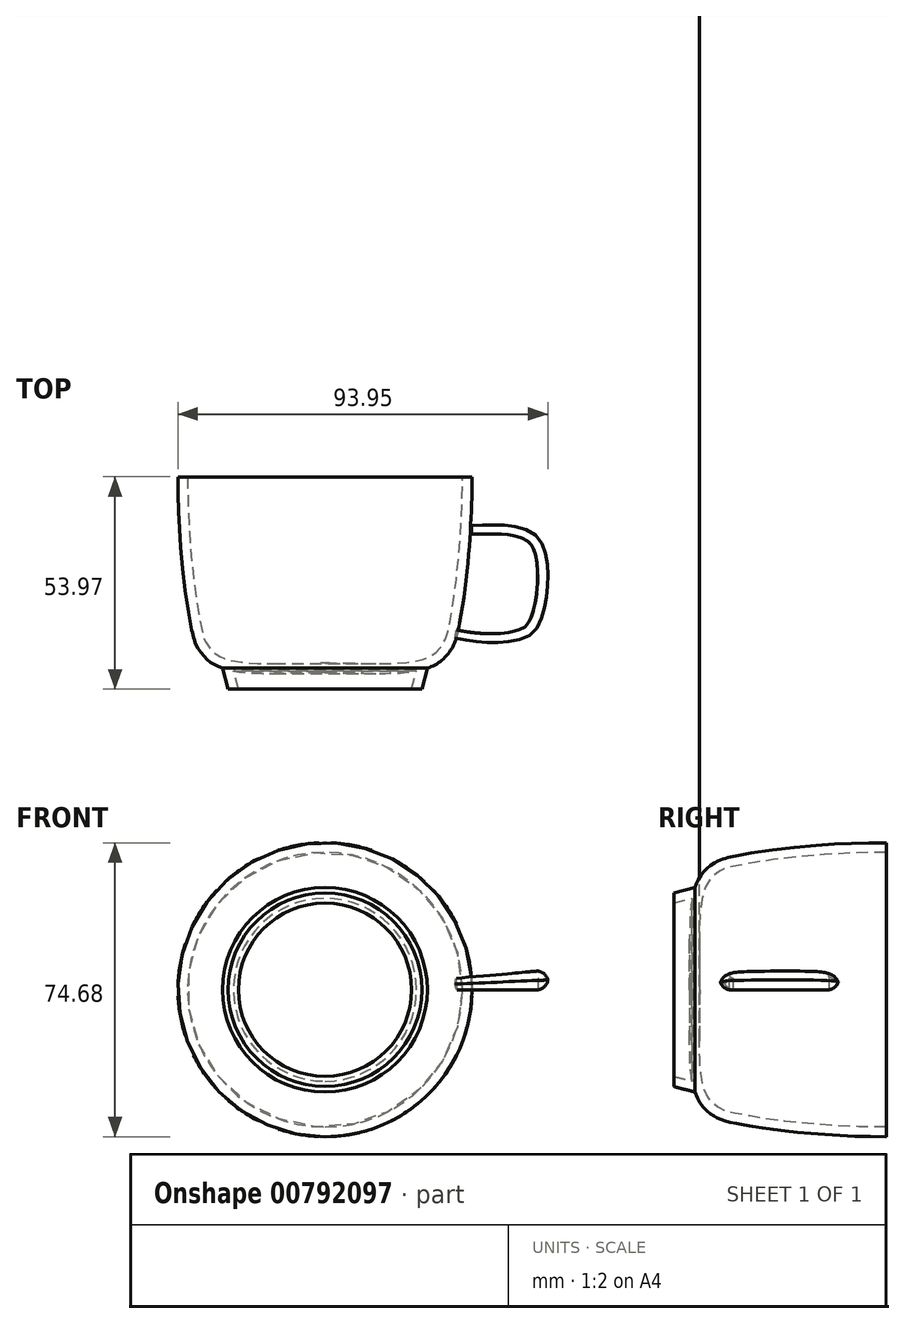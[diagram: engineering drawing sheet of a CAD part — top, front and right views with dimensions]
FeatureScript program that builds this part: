
annotation { "Feature Type Name" : "Feature", "Feature Type Description" : "" }
export const myFeature = defineFeature(function(context is Context, id is Id, definition is map)
    precondition{}
    {
        {
            var Q0;
            Q0=qCreatedBy(makeId("Top.planeOp"),FACE);
            var sketch = newSketch(context, id + "F0", { "sketchPlane" : qUnion([Q0])});
            skFitSpline(sketch, "E0", {"points": [v(0, -45.68) * mm, v(26, -44.55) * mm, v(31.9, -40.05) * mm, v(33.87, -34.71) * mm, v(37.24, 9.7) * mm], "startDerivative": vector(96.2, 0) * mm, "endDerivative": vector(-4.8, 143.62) * mm});
            skFitSpline(sketch, "E1.0", {"points": [v(0, -43.18) * mm, v(2.03, -43.18) * mm, v(6.14, -43.25) * mm, v(11.15, -43.35) * mm, v(14.93, -43.35) * mm, v(17.6, -43.29) * mm, v(20.07, -43.13) * mm, v(21.92, -42.92) * mm, v(23.24, -42.7) * mm, v(24.15, -42.5) * mm, v(24.97, -42.27) * mm, v(25.92, -41.93) * mm, v(26.94, -41.44) * mm, v(27.92, -40.78) * mm, v(28.59, -40.18) * mm, v(29.05, -39.69) * mm, v(29.37, -39.3) * mm, v(29.65, -38.92) * mm, v(29.91, -38.53) * mm, v(30.13, -38.17) * mm, v(30.39, -37.7) * mm, v(30.66, -37.1) * mm, v(30.97, -36.14) * mm, v(31.3, -34.83) * mm, v(31.66, -33.08) * mm, v(32.05, -30.94) * mm, v(32.6, -27.6) * mm, v(33.3, -22.6) * mm, v(34.03, -15.54) * mm, v(34.6, -7.66) * mm, v(34.89, 0.8) * mm, v(34.84, 6.66) * mm, v(34.74, 9.61) * mm]});
            skLineSegment(sketch, "E2", {"start": v(34.84, 4.08) * mm, "end": v(37.34, 4.08) * mm});
            skLineSegment(sketch, "E3", {"start": v(0, -49.9) * mm, "end": v(0, -43.18) * mm});
            skFitSpline(sketch, "E4", {"points": [v(0, -49.9) * mm, v(24.6, -49.9) * mm], "startDerivative": vector(24.6, 0) * mm, "endDerivative": vector(24.6, 0) * mm});
            skLineSegment(sketch, "E5", {"start": v(26, -44.55) * mm, "end": v(24.6, -49.9) * mm});
            skSolve(sketch);
        }
        {
            var Q0;
            {var subQ1=sQuery(id+"F0.wireOp",EDGE,"E0");var subQ5=sQuery(id+"F0.wireOp",EDGE,"E3");var subQ8=makeQuery(id+"F0.imprint","INTERSECT",VERTEX,{"derivedFrom":[subQ1,subQ5]});Q0=makeQuery(id+"F0.imprint","IMPRINT",FACE,{"disambiguationData":[TD([[makeQuery(id+"F0.imprint","IMPRINT",EDGE,{"disambiguationData":[TD([[subQ8,-1.0]])],"derivedFrom":subQ1}),1.0]])]});}
            var Q1;
            {var subQ4=sQuery(id+"F0.wireOp",EDGE,"E4");Q1=makeQuery(id+"F0.imprint","IMPRINT",FACE,{"disambiguationData":[TD([[makeQuery(id+"F0.imprint","IMPRINT",EDGE,{"derivedFrom":subQ4}),1.0]])]});}
            var Q2;
            Q2=sQuery(id+"F0.wireOp",EDGE,"E3");
            revolve(context, id + "F1", {"surfaceOperationType" : NewSurfaceOperationType.NEW, "entities" : qUnion([Q0, Q1]), "axis" : qUnion([Q2]), "revolveType" : RevolveType.FULL});
        }
        {
            var Q0;
            Q0=makeQuery(id+"F1.opRevolve","SWEPT_FACE",FACE,{"disambiguationData":[OSD([sQuery(id+"F0.wireOp",EDGE,"E4")])]});
            shell(context, id + "F2", {"entities" : qUnion([Q0]), "thickness" : 2.5 * mm});
        }
        {
            var Q0;
            Q0=qCreatedBy(makeId("Top.planeOp"),FACE);
            var sketch = newSketch(context, id + "F3", { "sketchPlane" : qUnion([Q0])});
            skFitSpline(sketch, "E6", {"points": [v(37.24, -8.01) * mm, v(49.05, -8.57) * mm, v(55.23, -12.79) * mm, v(54.67, -33.03) * mm, v(49.05, -37.52) * mm, v(33.03, -37.24) * mm], "startDerivative": vector(118.58, 3.49) * mm, "endDerivative": vector(-91.42, 18.28) * mm});
            skFitSpline(sketch, "E7.0", {"points": [v(37.32, -10.5) * mm, v(38.54, -10.47) * mm, v(40.68, -10.42) * mm, v(43.08, -10.4) * mm, v(44.83, -10.44) * mm, v(46.1, -10.54) * mm, v(46.92, -10.66) * mm, v(47.56, -10.79) * mm, v(47.98, -10.88) * mm, v(48.34, -10.97) * mm, v(48.72, -11.07) * mm, v(49.2, -11.2) * mm, v(49.74, -11.36) * mm, v(50.45, -11.61) * mm, v(51.26, -12) * mm, v(51.95, -12.51) * mm, v(52.43, -13.03) * mm, v(52.71, -13.41) * mm, v(52.93, -13.77) * mm, v(53.13, -14.16) * mm, v(53.37, -14.76) * mm, v(53.64, -15.63) * mm, v(53.93, -16.95) * mm, v(54.18, -18.85) * mm, v(54.26, -21.37) * mm, v(54.15, -23.98) * mm, v(53.86, -26.56) * mm, v(53.48, -28.55) * mm, v(53.11, -29.97) * mm, v(52.81, -30.93) * mm, v(52.5, -31.77) * mm, v(52.18, -32.46) * mm, v(51.86, -33) * mm, v(51.45, -33.58) * mm, v(50.94, -34.08) * mm, v(50.24, -34.52) * mm, v(49.43, -34.83) * mm, v(48.72, -35.03) * mm, v(48.27, -35.14) * mm, v(47.59, -35.3) * mm, v(46.47, -35.5) * mm, v(44.8, -35.69) * mm, v(42.93, -35.77) * mm, v(40.88, -35.74) * mm, v(37.89, -35.53) * mm, v(35.35, -35.16) * mm, v(33.52, -34.8) * mm]});
            skLineSegment(sketch, "E8", {"start": v(37.24, -8.01) * mm, "end": v(37.32, -10.5) * mm});
            skLineSegment(sketch, "E9", {"start": v(33.52, -34.8) * mm, "end": v(33.03, -37.24) * mm});
            skSolve(sketch);
        }
        {
            var Q0;
            Q0=makeQuery(id+"F3.imprint","IMPRINT",FACE,{"disambiguationData":[TD([[makeQuery(id+"F3.imprint","IMPRINT",EDGE,{"derivedFrom":sQuery(id+"F3.wireOp",EDGE,"E6")}),-1.0]])]});
            var Q1;
            Q1=makeQuery(id+"F1.opRevolve","SWEPT_FACE",FACE,{"disambiguationData":[OSD([sQuery(id+"F0.wireOp",EDGE,"E0")])]});
            revolve(context, id + "F4", {"surfaceOperationType" : NewSurfaceOperationType.NEW, "entities" : qUnion([Q0]), "axis" : qUnion([Q1]), "revolveType" : RevolveType.ONE_DIRECTION, "angle" : 5 * degree});
        }
        {
            var Q0;
            Q0=makeQuery(id+"F4.opRevolve","CAP_EDGE",EDGE,{"disambiguationData":[OSD([sQuery(id+"F3.wireOp",EDGE,"E6")])],"isStart":true});
            var Q1;
            Q1=makeQuery(id+"F4.opRevolve","CAP_EDGE",EDGE,{"disambiguationData":[OSD([sQuery(id+"F3.wireOp",EDGE,"E6")])],"isStart":false});
            fillet(context, id + "F5", {"entities" : qUnion([Q0, Q1]), "radius" : 3 * mm, "tangentPropagation" : true, "allowEdgeOverflow" : false});
        }
        {
            var Q0;
            Q0=qCreatedBy(makeId("Top.planeOp"),FACE);
            var sketch = newSketch(context, id + "F6", { "sketchPlane" : qUnion([Q0])});
            skText(sketch, "E10", { "text": "sgw", "fontName": "OpenSans-Regular.ttf"});
            const initialGuessF6  = {"E10": [-0.017, -0.03303, 1, 0, 0.01799]};
            skSetInitialGuess(sketch, initialGuessF6);
            skSolve(sketch);
        }
        {
            var Q0;
            Q0 = qSketchRegion(id + "F6", true);
            extrude(context, id + "F7", {"entities" : qUnion([Q0]), "depth" : 36 * mm, "offsetDistance" : 25 * mm});
        }
        {
            var Q0;
            Q0=makeQuery(id+"F1.opRevolve","SWEPT_BODY",BODY,{"disambiguationData":[OSD([sQuery(id+"F0.wireOp",EDGE,"E0"),sQuery(id+"F0.wireOp",EDGE,"E1.0"),sQuery(id+"F0.wireOp",EDGE,"E2"),sQuery(id+"F0.wireOp",EDGE,"E3"),sQuery(id+"F0.wireOp",EDGE,"E4"),sQuery(id+"F0.wireOp",EDGE,"E5")])]});
            var Q1;
            Q1=makeQuery(id+"F7.opExtrude","SWEPT_BODY",BODY,{"disambiguationData":[OSD([sQuery(id+"F6.wireOp",EDGE,"E10.sketch_text.stroke-69"),sQuery(id+"F6.wireOp",EDGE,"E10.sketch_text.stroke-70"),sQuery(id+"F6.wireOp",EDGE,"E10.sketch_text.stroke-71"),sQuery(id+"F6.wireOp",EDGE,"E10.sketch_text.stroke-72"),sQuery(id+"F6.wireOp",EDGE,"E10.sketch_text.stroke-73"),sQuery(id+"F6.wireOp",EDGE,"E10.sketch_text.stroke-74"),sQuery(id+"F6.wireOp",EDGE,"E10.sketch_text.stroke-75"),sQuery(id+"F6.wireOp",EDGE,"E10.sketch_text.stroke-76"),sQuery(id+"F6.wireOp",EDGE,"E10.sketch_text.stroke-77"),sQuery(id+"F6.wireOp",EDGE,"E10.sketch_text.stroke-78"),sQuery(id+"F6.wireOp",EDGE,"E10.sketch_text.stroke-79"),sQuery(id+"F6.wireOp",EDGE,"E10.sketch_text.stroke-80"),sQuery(id+"F6.wireOp",EDGE,"E10.sketch_text.stroke-81"),sQuery(id+"F6.wireOp",EDGE,"E10.sketch_text.stroke-82"),sQuery(id+"F6.wireOp",EDGE,"E10.sketch_text.stroke-83"),sQuery(id+"F6.wireOp",EDGE,"E10.sketch_text.stroke-84"),sQuery(id+"F6.wireOp",EDGE,"E10.sketch_text.stroke-85"),sQuery(id+"F6.wireOp",EDGE,"E10.sketch_text.stroke-86"),sQuery(id+"F6.wireOp",EDGE,"E10.sketch_text.stroke-87"),sQuery(id+"F6.wireOp",EDGE,"E10.sketch_text.stroke-88"),sQuery(id+"F6.wireOp",EDGE,"E10.sketch_text.stroke-89"),sQuery(id+"F6.wireOp",EDGE,"E10.sketch_text.stroke-90"),sQuery(id+"F6.wireOp",EDGE,"E10.sketch_text.stroke-91")])]});
            var Q2;
            Q2=makeQuery(id+"F7.opExtrude","SWEPT_BODY",BODY,{"disambiguationData":[OSD([sQuery(id+"F6.wireOp",EDGE,"E10.sketch_text.stroke-25"),sQuery(id+"F6.wireOp",EDGE,"E10.sketch_text.stroke-26"),sQuery(id+"F6.wireOp",EDGE,"E10.sketch_text.stroke-27"),sQuery(id+"F6.wireOp",EDGE,"E10.sketch_text.stroke-28"),sQuery(id+"F6.wireOp",EDGE,"E10.sketch_text.stroke-29"),sQuery(id+"F6.wireOp",EDGE,"E10.sketch_text.stroke-30"),sQuery(id+"F6.wireOp",EDGE,"E10.sketch_text.stroke-31"),sQuery(id+"F6.wireOp",EDGE,"E10.sketch_text.stroke-32"),sQuery(id+"F6.wireOp",EDGE,"E10.sketch_text.stroke-33"),sQuery(id+"F6.wireOp",EDGE,"E10.sketch_text.stroke-34"),sQuery(id+"F6.wireOp",EDGE,"E10.sketch_text.stroke-35"),sQuery(id+"F6.wireOp",EDGE,"E10.sketch_text.stroke-36"),sQuery(id+"F6.wireOp",EDGE,"E10.sketch_text.stroke-37"),sQuery(id+"F6.wireOp",EDGE,"E10.sketch_text.stroke-38"),sQuery(id+"F6.wireOp",EDGE,"E10.sketch_text.stroke-39"),sQuery(id+"F6.wireOp",EDGE,"E10.sketch_text.stroke-40"),sQuery(id+"F6.wireOp",EDGE,"E10.sketch_text.stroke-41"),sQuery(id+"F6.wireOp",EDGE,"E10.sketch_text.stroke-42"),sQuery(id+"F6.wireOp",EDGE,"E10.sketch_text.stroke-43"),sQuery(id+"F6.wireOp",EDGE,"E10.sketch_text.stroke-44"),sQuery(id+"F6.wireOp",EDGE,"E10.sketch_text.stroke-45"),sQuery(id+"F6.wireOp",EDGE,"E10.sketch_text.stroke-46"),sQuery(id+"F6.wireOp",EDGE,"E10.sketch_text.stroke-47"),sQuery(id+"F6.wireOp",EDGE,"E10.sketch_text.stroke-48"),sQuery(id+"F6.wireOp",EDGE,"E10.sketch_text.stroke-49"),sQuery(id+"F6.wireOp",EDGE,"E10.sketch_text.stroke-50"),sQuery(id+"F6.wireOp",EDGE,"E10.sketch_text.stroke-51"),sQuery(id+"F6.wireOp",EDGE,"E10.sketch_text.stroke-52"),sQuery(id+"F6.wireOp",EDGE,"E10.sketch_text.stroke-53"),sQuery(id+"F6.wireOp",EDGE,"E10.sketch_text.stroke-54"),sQuery(id+"F6.wireOp",EDGE,"E10.sketch_text.stroke-55"),sQuery(id+"F6.wireOp",EDGE,"E10.sketch_text.stroke-56"),sQuery(id+"F6.wireOp",EDGE,"E10.sketch_text.stroke-57"),sQuery(id+"F6.wireOp",EDGE,"E10.sketch_text.stroke-58"),sQuery(id+"F6.wireOp",EDGE,"E10.sketch_text.stroke-59"),sQuery(id+"F6.wireOp",EDGE,"E10.sketch_text.stroke-60"),sQuery(id+"F6.wireOp",EDGE,"E10.sketch_text.stroke-61"),sQuery(id+"F6.wireOp",EDGE,"E10.sketch_text.stroke-62"),sQuery(id+"F6.wireOp",EDGE,"E10.sketch_text.stroke-63"),sQuery(id+"F6.wireOp",EDGE,"E10.sketch_text.stroke-64"),sQuery(id+"F6.wireOp",EDGE,"E10.sketch_text.stroke-65"),sQuery(id+"F6.wireOp",EDGE,"E10.sketch_text.stroke-66"),sQuery(id+"F6.wireOp",EDGE,"E10.sketch_text.stroke-67"),sQuery(id+"F6.wireOp",EDGE,"E10.sketch_text.stroke-68")])]});
            var Q3;
            Q3=makeQuery(id+"F7.opExtrude","SWEPT_BODY",BODY,{"disambiguationData":[OSD([sQuery(id+"F6.wireOp",EDGE,"E10.sketch_text.stroke-0"),sQuery(id+"F6.wireOp",EDGE,"E10.sketch_text.stroke-1"),sQuery(id+"F6.wireOp",EDGE,"E10.sketch_text.stroke-2"),sQuery(id+"F6.wireOp",EDGE,"E10.sketch_text.stroke-3"),sQuery(id+"F6.wireOp",EDGE,"E10.sketch_text.stroke-4"),sQuery(id+"F6.wireOp",EDGE,"E10.sketch_text.stroke-5"),sQuery(id+"F6.wireOp",EDGE,"E10.sketch_text.stroke-6"),sQuery(id+"F6.wireOp",EDGE,"E10.sketch_text.stroke-7"),sQuery(id+"F6.wireOp",EDGE,"E10.sketch_text.stroke-8"),sQuery(id+"F6.wireOp",EDGE,"E10.sketch_text.stroke-9"),sQuery(id+"F6.wireOp",EDGE,"E10.sketch_text.stroke-10"),sQuery(id+"F6.wireOp",EDGE,"E10.sketch_text.stroke-11"),sQuery(id+"F6.wireOp",EDGE,"E10.sketch_text.stroke-12"),sQuery(id+"F6.wireOp",EDGE,"E10.sketch_text.stroke-13"),sQuery(id+"F6.wireOp",EDGE,"E10.sketch_text.stroke-14"),sQuery(id+"F6.wireOp",EDGE,"E10.sketch_text.stroke-15"),sQuery(id+"F6.wireOp",EDGE,"E10.sketch_text.stroke-16"),sQuery(id+"F6.wireOp",EDGE,"E10.sketch_text.stroke-17"),sQuery(id+"F6.wireOp",EDGE,"E10.sketch_text.stroke-18"),sQuery(id+"F6.wireOp",EDGE,"E10.sketch_text.stroke-19"),sQuery(id+"F6.wireOp",EDGE,"E10.sketch_text.stroke-20"),sQuery(id+"F6.wireOp",EDGE,"E10.sketch_text.stroke-21"),sQuery(id+"F6.wireOp",EDGE,"E10.sketch_text.stroke-22"),sQuery(id+"F6.wireOp",EDGE,"E10.sketch_text.stroke-23"),sQuery(id+"F6.wireOp",EDGE,"E10.sketch_text.stroke-24")])]});
            booleanBodies(context, id + "F8", {"operationType" : BooleanOperationType.SUBTRACTION, "tools" : qUnion([Q0]), "targets" : qUnion([Q1, Q2, Q3]), "keepTools" : true});
        }
        {
            var Q0;
            Q0=makeQuery(id+"F8.opBoolean","SPLIT",BODY,{"disambiguationData":[OD(0.0)],"derivedFrom":makeQuery(id+"F7.opExtrude","SWEPT_BODY",BODY,{"disambiguationData":[OSD([sQuery(id+"F6.wireOp",EDGE,"E10.sketch_text.stroke-0"),sQuery(id+"F6.wireOp",EDGE,"E10.sketch_text.stroke-1"),sQuery(id+"F6.wireOp",EDGE,"E10.sketch_text.stroke-2"),sQuery(id+"F6.wireOp",EDGE,"E10.sketch_text.stroke-3"),sQuery(id+"F6.wireOp",EDGE,"E10.sketch_text.stroke-4"),sQuery(id+"F6.wireOp",EDGE,"E10.sketch_text.stroke-5"),sQuery(id+"F6.wireOp",EDGE,"E10.sketch_text.stroke-6"),sQuery(id+"F6.wireOp",EDGE,"E10.sketch_text.stroke-7"),sQuery(id+"F6.wireOp",EDGE,"E10.sketch_text.stroke-8"),sQuery(id+"F6.wireOp",EDGE,"E10.sketch_text.stroke-9"),sQuery(id+"F6.wireOp",EDGE,"E10.sketch_text.stroke-10"),sQuery(id+"F6.wireOp",EDGE,"E10.sketch_text.stroke-11"),sQuery(id+"F6.wireOp",EDGE,"E10.sketch_text.stroke-12"),sQuery(id+"F6.wireOp",EDGE,"E10.sketch_text.stroke-13"),sQuery(id+"F6.wireOp",EDGE,"E10.sketch_text.stroke-14"),sQuery(id+"F6.wireOp",EDGE,"E10.sketch_text.stroke-15"),sQuery(id+"F6.wireOp",EDGE,"E10.sketch_text.stroke-16"),sQuery(id+"F6.wireOp",EDGE,"E10.sketch_text.stroke-17"),sQuery(id+"F6.wireOp",EDGE,"E10.sketch_text.stroke-18"),sQuery(id+"F6.wireOp",EDGE,"E10.sketch_text.stroke-19"),sQuery(id+"F6.wireOp",EDGE,"E10.sketch_text.stroke-20"),sQuery(id+"F6.wireOp",EDGE,"E10.sketch_text.stroke-21"),sQuery(id+"F6.wireOp",EDGE,"E10.sketch_text.stroke-22"),sQuery(id+"F6.wireOp",EDGE,"E10.sketch_text.stroke-23"),sQuery(id+"F6.wireOp",EDGE,"E10.sketch_text.stroke-24")])]})});
            var Q1;
            Q1=makeQuery(id+"F8.opBoolean","SPLIT",BODY,{"disambiguationData":[OD(0.0)],"derivedFrom":makeQuery(id+"F7.opExtrude","SWEPT_BODY",BODY,{"disambiguationData":[OSD([sQuery(id+"F6.wireOp",EDGE,"E10.sketch_text.stroke-25"),sQuery(id+"F6.wireOp",EDGE,"E10.sketch_text.stroke-26"),sQuery(id+"F6.wireOp",EDGE,"E10.sketch_text.stroke-27"),sQuery(id+"F6.wireOp",EDGE,"E10.sketch_text.stroke-28"),sQuery(id+"F6.wireOp",EDGE,"E10.sketch_text.stroke-29"),sQuery(id+"F6.wireOp",EDGE,"E10.sketch_text.stroke-30"),sQuery(id+"F6.wireOp",EDGE,"E10.sketch_text.stroke-31"),sQuery(id+"F6.wireOp",EDGE,"E10.sketch_text.stroke-32"),sQuery(id+"F6.wireOp",EDGE,"E10.sketch_text.stroke-33"),sQuery(id+"F6.wireOp",EDGE,"E10.sketch_text.stroke-34"),sQuery(id+"F6.wireOp",EDGE,"E10.sketch_text.stroke-35"),sQuery(id+"F6.wireOp",EDGE,"E10.sketch_text.stroke-36"),sQuery(id+"F6.wireOp",EDGE,"E10.sketch_text.stroke-37"),sQuery(id+"F6.wireOp",EDGE,"E10.sketch_text.stroke-38"),sQuery(id+"F6.wireOp",EDGE,"E10.sketch_text.stroke-39"),sQuery(id+"F6.wireOp",EDGE,"E10.sketch_text.stroke-40"),sQuery(id+"F6.wireOp",EDGE,"E10.sketch_text.stroke-41"),sQuery(id+"F6.wireOp",EDGE,"E10.sketch_text.stroke-42"),sQuery(id+"F6.wireOp",EDGE,"E10.sketch_text.stroke-43"),sQuery(id+"F6.wireOp",EDGE,"E10.sketch_text.stroke-44"),sQuery(id+"F6.wireOp",EDGE,"E10.sketch_text.stroke-45"),sQuery(id+"F6.wireOp",EDGE,"E10.sketch_text.stroke-46"),sQuery(id+"F6.wireOp",EDGE,"E10.sketch_text.stroke-47"),sQuery(id+"F6.wireOp",EDGE,"E10.sketch_text.stroke-48"),sQuery(id+"F6.wireOp",EDGE,"E10.sketch_text.stroke-49"),sQuery(id+"F6.wireOp",EDGE,"E10.sketch_text.stroke-50"),sQuery(id+"F6.wireOp",EDGE,"E10.sketch_text.stroke-51"),sQuery(id+"F6.wireOp",EDGE,"E10.sketch_text.stroke-52"),sQuery(id+"F6.wireOp",EDGE,"E10.sketch_text.stroke-53"),sQuery(id+"F6.wireOp",EDGE,"E10.sketch_text.stroke-54"),sQuery(id+"F6.wireOp",EDGE,"E10.sketch_text.stroke-55"),sQuery(id+"F6.wireOp",EDGE,"E10.sketch_text.stroke-56"),sQuery(id+"F6.wireOp",EDGE,"E10.sketch_text.stroke-57"),sQuery(id+"F6.wireOp",EDGE,"E10.sketch_text.stroke-58"),sQuery(id+"F6.wireOp",EDGE,"E10.sketch_text.stroke-59"),sQuery(id+"F6.wireOp",EDGE,"E10.sketch_text.stroke-60"),sQuery(id+"F6.wireOp",EDGE,"E10.sketch_text.stroke-61"),sQuery(id+"F6.wireOp",EDGE,"E10.sketch_text.stroke-62"),sQuery(id+"F6.wireOp",EDGE,"E10.sketch_text.stroke-63"),sQuery(id+"F6.wireOp",EDGE,"E10.sketch_text.stroke-64"),sQuery(id+"F6.wireOp",EDGE,"E10.sketch_text.stroke-65"),sQuery(id+"F6.wireOp",EDGE,"E10.sketch_text.stroke-66"),sQuery(id+"F6.wireOp",EDGE,"E10.sketch_text.stroke-67"),sQuery(id+"F6.wireOp",EDGE,"E10.sketch_text.stroke-68")])]})});
            var Q2;
            Q2=makeQuery(id+"F8.opBoolean","SPLIT",BODY,{"disambiguationData":[OD(0.0)],"derivedFrom":makeQuery(id+"F7.opExtrude","SWEPT_BODY",BODY,{"disambiguationData":[OSD([sQuery(id+"F6.wireOp",EDGE,"E10.sketch_text.stroke-69"),sQuery(id+"F6.wireOp",EDGE,"E10.sketch_text.stroke-70"),sQuery(id+"F6.wireOp",EDGE,"E10.sketch_text.stroke-71"),sQuery(id+"F6.wireOp",EDGE,"E10.sketch_text.stroke-72"),sQuery(id+"F6.wireOp",EDGE,"E10.sketch_text.stroke-73"),sQuery(id+"F6.wireOp",EDGE,"E10.sketch_text.stroke-74"),sQuery(id+"F6.wireOp",EDGE,"E10.sketch_text.stroke-75"),sQuery(id+"F6.wireOp",EDGE,"E10.sketch_text.stroke-76"),sQuery(id+"F6.wireOp",EDGE,"E10.sketch_text.stroke-77"),sQuery(id+"F6.wireOp",EDGE,"E10.sketch_text.stroke-78"),sQuery(id+"F6.wireOp",EDGE,"E10.sketch_text.stroke-79"),sQuery(id+"F6.wireOp",EDGE,"E10.sketch_text.stroke-80"),sQuery(id+"F6.wireOp",EDGE,"E10.sketch_text.stroke-81"),sQuery(id+"F6.wireOp",EDGE,"E10.sketch_text.stroke-82"),sQuery(id+"F6.wireOp",EDGE,"E10.sketch_text.stroke-83"),sQuery(id+"F6.wireOp",EDGE,"E10.sketch_text.stroke-84"),sQuery(id+"F6.wireOp",EDGE,"E10.sketch_text.stroke-85"),sQuery(id+"F6.wireOp",EDGE,"E10.sketch_text.stroke-86"),sQuery(id+"F6.wireOp",EDGE,"E10.sketch_text.stroke-87"),sQuery(id+"F6.wireOp",EDGE,"E10.sketch_text.stroke-88"),sQuery(id+"F6.wireOp",EDGE,"E10.sketch_text.stroke-89"),sQuery(id+"F6.wireOp",EDGE,"E10.sketch_text.stroke-90"),sQuery(id+"F6.wireOp",EDGE,"E10.sketch_text.stroke-91")])]})});
            deleteBodies(context, id + "F9", {"entities" : qUnion([Q0, Q1, Q2])});
        }
    });
